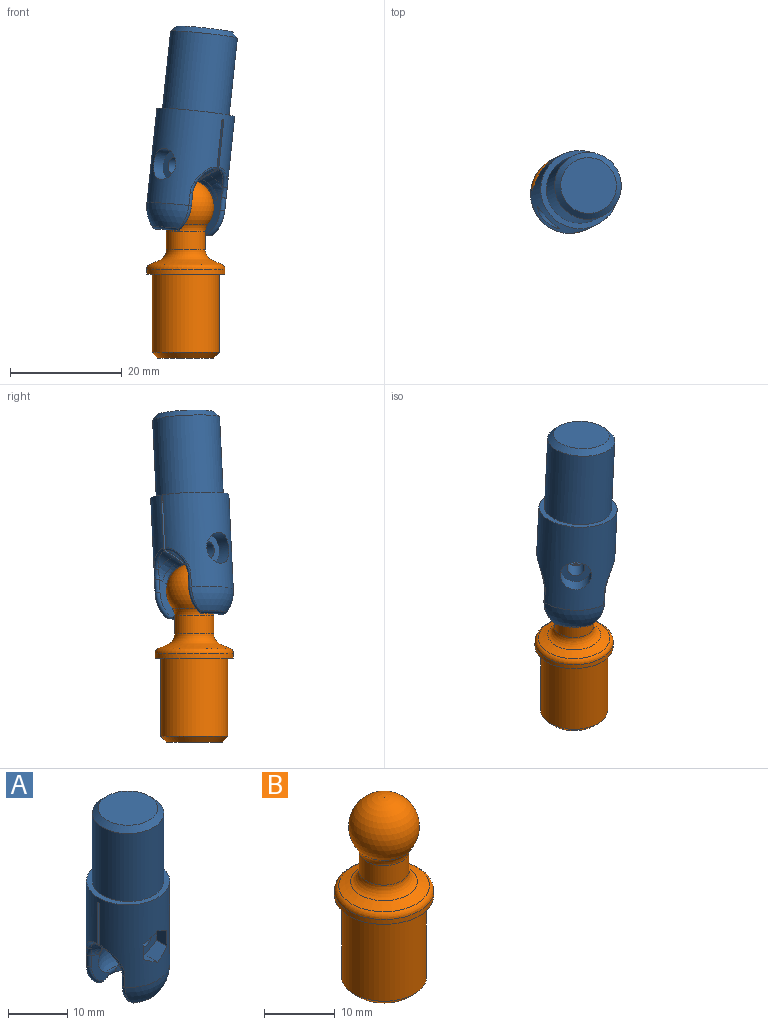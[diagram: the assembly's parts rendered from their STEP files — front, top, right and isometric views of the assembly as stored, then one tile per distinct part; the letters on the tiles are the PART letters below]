
ASSEMBLY  parts=2 mates=1
PART A: 85 faces, bbox 15.2x14.1x37.4 mm
  f0: bspline ~4.01x3.5mm, area 9.6mm2, adj f1,f43,f46,f64,f70
  f1: bspline ~3.61x3.5mm, area 5.3mm2, adj f0,f2,f43,f46
  f2: bspline ~3.5x3.22mm, area 0.4mm2, adj f1,f3,f43,f45
  f3: bspline ~3.23x3.19mm, area 0.4mm2, adj f2,f4,f43,f45
  f4: bspline ~3.24x2.96mm, area 0.3mm2, adj f3,f5,f43,f45
  f5: bspline ~3.22x2.78mm, area 2.6mm2, adj f4,f26,f37,f45
  f6: bspline ~4.01x3.5mm, area 9.6mm2, adj f7,f24,f30,f46,f73
  f7: bspline ~3.61x3.5mm, area 5.3mm2, adj f6,f8,f30,f46
  f8: bspline ~3.5x3.22mm, area 0.4mm2, adj f7,f9,f30,f45
  f9: bspline ~3.23x3.19mm, area 0.4mm2, adj f8,f10,f30,f45
  f10: bspline ~3.24x2.97mm, area 0.3mm2, adj f9,f11,f30,f45
  f11: bspline ~3.22x2.78mm, area 2.6mm2, adj f10,f27,f37,f45
  f12: bspline ~4.01x3.5mm, area 9.6mm2, adj f13,f25,f44,f47,f77
  f13: bspline ~3.61x3.5mm, area 5.3mm2, adj f12,f14,f44,f47
  f14: bspline ~3.5x3.22mm, area 0.4mm2, adj f13,f15,f33,f44
  f15: bspline ~3.23x3.19mm, area 0.4mm2, adj f14,f16,f33,f44
  f16: bspline ~3.24x2.96mm, area 0.3mm2, adj f15,f17,f33,f44
  f17: bspline ~3.22x2.78mm, area 2.6mm2, adj f16,f28,f33,f34
  f18: bspline ~4.01x3.5mm, area 9.6mm2, adj f19,f31,f47,f61,f82
  f19: bspline ~3.61x3.5mm, area 5.3mm2, adj f18,f20,f31,f47
  f20: bspline ~3.5x3.22mm, area 0.4mm2, adj f19,f21,f31,f33
  f21: bspline ~3.23x3.19mm, area 0.4mm2, adj f20,f22,f31,f33
  f22: bspline ~3.24x2.97mm, area 0.3mm2, adj f21,f23,f31,f33
  f23: bspline ~3.22x2.78mm, area 2.6mm2, adj f22,f29,f33,f34
  f24: cylinder r=3.5mm len=3.18mm, axis (-0.91,0,0.42), area 5mm2, adj f6,f46,f74
  f25: cylinder r=3.5mm len=3.18mm, axis (0.91,0,0.42), area 5mm2, adj f12,f47,f78
  f26: bspline ~1.83x1.63mm, area 2.2mm2, adj f5,f37,f45,f65
  f27: bspline ~1.83x1.63mm, area 2.2mm2, adj f11,f37,f45,f66
  f28: bspline ~1.83x1.63mm, area 2.2mm2, adj f17,f33,f34,f62
  f29: bspline ~1.83x1.63mm, area 2.2mm2, adj f23,f33,f34,f63
  f30: plane 6.85x4.31mm, normal (0,1,0), area 11.6mm2, adj f6,f7,f8,f9,f10,f37,f38,f71
  f31: plane 6.85x4.31mm, normal (0,-1,0), area 11.6mm2, adj f18,f19,f20,f21,f22,f34,f35,f79
  f32: cylinder r=7mm len=17mm, axis (0,0,1), area 562.6mm2, adj f36,f39,f40,f46,f47,f48,f49,f54
  f33: sphere r=5mm, area 7.6mm2, adj f14,f15,f16,f17,f20,f21,f22,f23
  f34: sphere r=5mm, area 38.4mm2, adj f17,f23,f28,f29,f31,f35,f44,f62
  f35: torus R=4.82mm, axis (0,0,1), area 12.9mm2, adj f31,f34,f36,f44,f75,f79
  f36: sphere r=7mm, area 43.4mm2, adj f32,f35,f75,f79
  f37: sphere r=5mm, area 38.4mm2, adj f5,f11,f26,f27,f30,f38,f43,f65
  f38: torus R=4.82mm, axis (0,0,1), area 12.9mm2, adj f30,f37,f39,f43,f67,f71
  f39: sphere r=7mm, area 43.4mm2, adj f32,f38,f67,f71
  f40: plane 14x14mm, normal (0,0,1), area 40.8mm2, adj f32,f41
  f41: cylinder r=6mm len=14mm, axis (0,0,1), area 527.8mm2, adj f40,f60
  f42: plane 10x10mm, normal (0,0,1), area 78.5mm2, adj f60
  f43: plane 6.85x4.31mm, normal (0,1,0), area 11.6mm2, adj f0,f1,f2,f3,f4,f37,f38,f67
  f44: plane 6.85x4.31mm, normal (0,-1,0), area 11.6mm2, adj f12,f13,f14,f15,f16,f34,f35,f75
  f45: sphere r=5mm, area 7.6mm2, adj f2,f3,f4,f5,f8,f9,f10,f11
  f46: plane 14x11.08mm, normal (0,1,0), area 131.7mm2, adj f0,f1,f6,f7,f24,f32,f45,f48
  f47: plane 14x11.08mm, normal (0,-1,0), area 131.7mm2, adj f12,f13,f18,f19,f25,f32,f33,f48
  f48: cylinder r=0.25mm len=14mm, axis (-1,0,0), area 11mm2, adj f32,f46,f47
  f49: cylinder r=2.8mm len=5.6mm, axis (0,1,0), area 52.8mm2, adj f32,f50
  f50: plane 5.6x5.6mm, normal (0,1,0), area 17.1mm2, adj f49,f51
  f51: cylinder r=1.55mm len=3.55mm, axis (0,1,0), area 34.6mm2, adj f50,f84
  f52: cylinder r=1.55mm len=3.55mm, axis (0,1,0), area 34.6mm2, adj f53,f83
  f53: plane 6.47x5.6mm, normal (0,-1,0), area 19.6mm2, adj f52,f54,f55,f56,f57,f58,f59
  f54: plane 3.23x2.42mm, normal (1,0,0), area 7.8mm2, adj f32,f53,f55,f59
  f55: plane 3.04x2.84mm, normal (0.5,0,0.87), area 9.1mm2, adj f32,f53,f54,f56
  f56: plane 3.04x2.84mm, normal (-0.5,0,0.87), area 9.1mm2, adj f32,f53,f55,f57
  f57: plane 3.23x2.42mm, normal (-1,0,0), area 7.8mm2, adj f32,f53,f56,f58
  f58: plane 3.04x2.84mm, normal (-0.5,0,-0.87), area 9.1mm2, adj f32,f53,f57,f59
  f59: plane 3.04x2.84mm, normal (0.5,0,-0.87), area 9.1mm2, adj f32,f53,f54,f58
  f60: cone r=5mm half-angle=45deg, axis (0,0,-1), area 48.9mm2, adj f41,f42
  f61: cylinder r=3.5mm len=3.18mm, axis (0.91,0,-0.42), area 5mm2, adj f18,f47,f81
  f62: bspline ~1.58x0.88mm, area 0.1mm2, adj f28,f34,f63
  f63: bspline ~1.58x0.88mm, area 0.1mm2, adj f29,f34,f62
  f64: cylinder r=3.5mm len=3.18mm, axis (-0.91,0,-0.42), area 5mm2, adj f0,f46,f69
  f65: bspline ~1.58x0.88mm, area 0.1mm2, adj f26,f37,f66
  f66: bspline ~1.58x0.88mm, area 0.1mm2, adj f27,f37,f65
  f67: torus R=4.92mm, axis (0,-1,0), area 6.1mm2, adj f38,f39,f43,f68
  f68: cylinder r=0.5mm len=2.29mm, axis (0,0,1), area 2.6mm2, adj f32,f43,f67,f70
  f69: bspline ~4.52x4.31mm, area 3.9mm2, adj f32,f46,f64,f70
  f70: bspline ~2.71x1.38mm, area 2mm2, adj f0,f32,f68,f69
  f71: torus R=4.92mm, axis (0,-1,0), area 6.1mm2, adj f30,f38,f39,f72
  f72: cylinder r=0.5mm len=2.29mm, axis (0,0,1), area 2.6mm2, adj f30,f32,f71,f73
  f73: bspline ~2.71x1.38mm, area 2mm2, adj f6,f32,f72,f74
  f74: bspline ~4.33x3.7mm, area 3.9mm2, adj f24,f32,f46,f73
  f75: torus R=4.92mm, axis (0,-1,0), area 6.1mm2, adj f35,f36,f44,f76
  f76: cylinder r=0.5mm len=2.29mm, axis (0,0,1), area 2.6mm2, adj f32,f44,f75,f77
  f77: bspline ~1.97x1.14mm, area 2mm2, adj f12,f32,f76,f78
  f78: bspline ~4.52x4.31mm, area 3.9mm2, adj f25,f32,f47,f77
  f79: torus R=4.92mm, axis (0,-1,0), area 6.1mm2, adj f31,f35,f36,f80
  f80: cylinder r=0.5mm len=2.29mm, axis (0,0,1), area 2.6mm2, adj f31,f32,f79,f82
  f81: bspline ~4.52x4.31mm, area 3.9mm2, adj f32,f47,f61,f82
  f82: bspline ~2.23x1.2mm, area 2mm2, adj f18,f32,f80,f81
  f83: torus R=1.75mm, axis (0,-1,0), area 3.2mm2, adj f46,f52
  f84: torus R=1.75mm, axis (0,-1,0), area 3.2mm2, adj f47,f51
PART B: 11 faces, bbox 15.2x15.2x32 mm
  f0: cylinder r=6mm len=14mm, axis (0,0,1), area 527.8mm2, adj f1,f7
  f1: plane 14x14mm, normal (0,0,-1), area 40.8mm2, adj f0,f2
  f2: cylinder r=7mm len=14mm, axis (0,0,1), area 37mm2, adj f1,f8
  f3: cone r=3.5mm half-angle=66.8deg, axis (0,0,-1), area 63.8mm2, adj f8,f10
  f4: cylinder r=3.5mm len=7mm, axis (0,0,1), area 73.7mm2, adj f9,f10
  f5: sphere r=5mm, area 254.2mm2, adj f9
  f6: plane 10x10mm, normal (0,0,-1), area 78.5mm2, adj f7
  f7: cone r=6mm half-angle=45deg, axis (0,0,1), area 48.9mm2, adj f0,f6
  f8: torus R=6mm, axis (0,0,-1), area 49.7mm2, adj f2,f3
  f9: torus R=5.5mm, axis (0,0,1), area 30.5mm2, adj f4,f5
  f10: torus R=5.5mm, axis (0,0,1), area 57.5mm2, adj f3,f4
PLACE A rot(axis=(0.04,0.04,1),135.3deg) t=(-1.26,-0.56,0.08)mm
PLACE B at identity fixed
MATE ball B.f10 <-> A.f35  axis (0,0,1) through (0,0,12)mm
